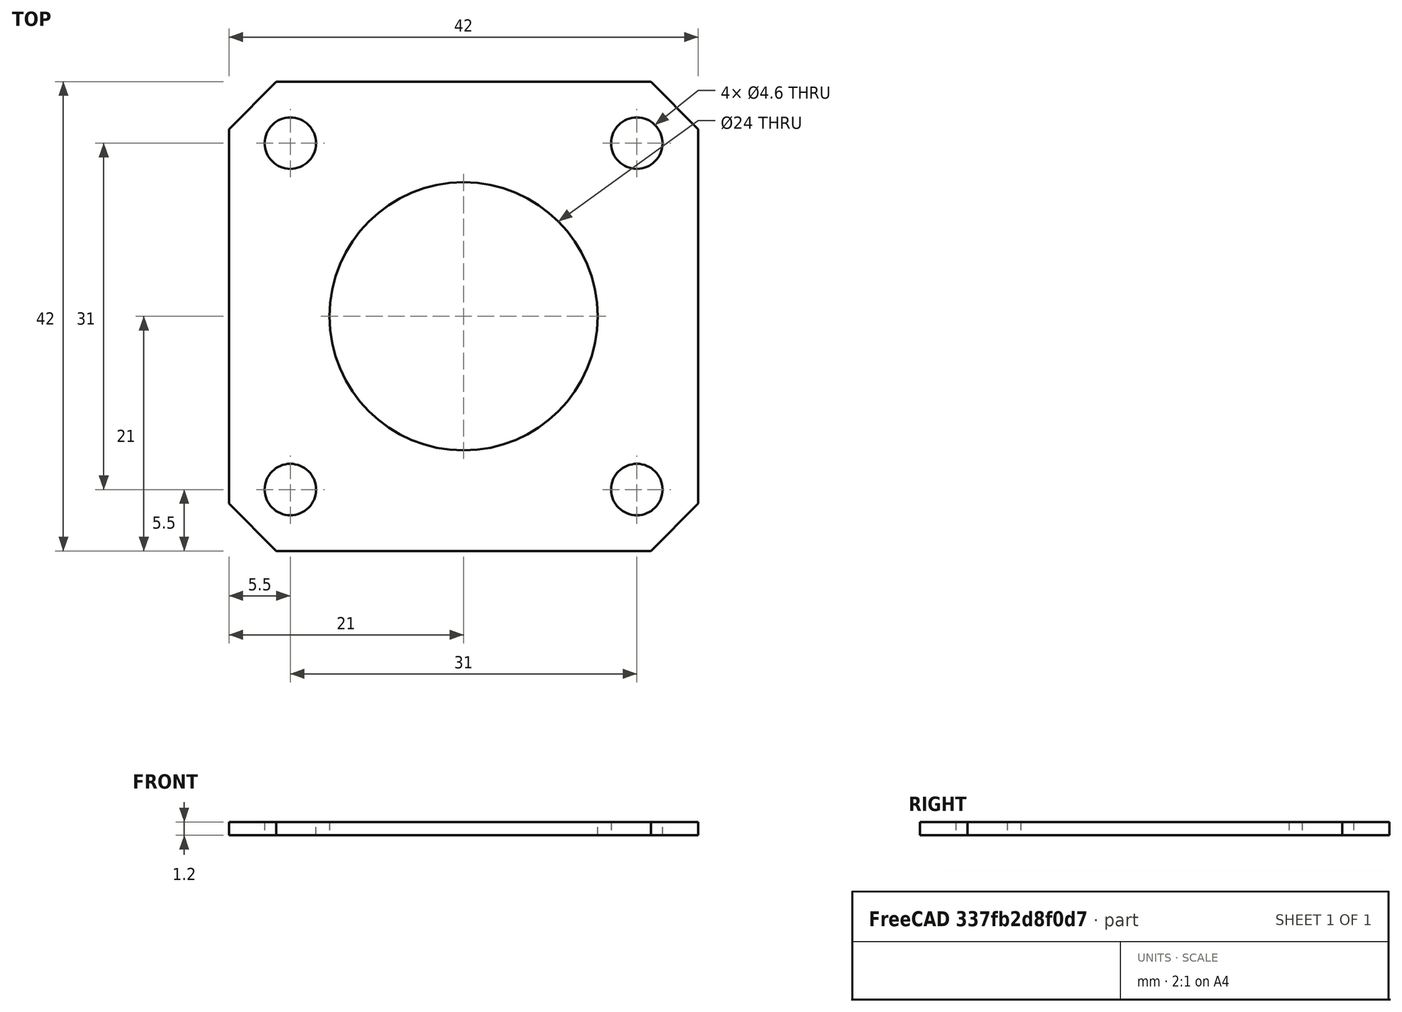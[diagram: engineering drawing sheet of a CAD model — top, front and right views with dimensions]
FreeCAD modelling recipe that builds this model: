
FCSTD DOCUMENT  (FreeCAD 0.20R28936 (Git))
Label: NEMA17_spacer
License: All rights reserved
LicenseURL: http://en.wikipedia.org/wiki/All_rights_reserved
objects: Sketcher::SketchObject×1, PartDesign::Pad×1, PartDesign::Body×1
note: 4 computed .brp shape members not serialized (recipe doc carries the construction recipe); baked Part::Feature solids carry a one-line shape summary decoded from their .brp

FEATURE [Sketcher::SketchObject] Sketch
  FullyConstrained = true
  MapMode = 5
  Support = -> [XY_Plane]
  sketch-geometry (21):
    g0: LineSegment StartX=-16.7574 StartY=21 StartZ=0 EndX=16.7574 EndY=21 EndZ=0
    g1: LineSegment StartX=21 StartY=16.7574 StartZ=0 EndX=21 EndY=-16.7574 EndZ=0
    g2: LineSegment StartX=16.7574 StartY=-21 StartZ=0 EndX=-16.7574 EndY=-21 EndZ=0
    g3: LineSegment StartX=-21 StartY=-16.7574 StartZ=0 EndX=-21 EndY=16.7574 EndZ=0
    g4: LineSegment StartX=-21 StartY=16.7574 StartZ=0 EndX=-16.7574 EndY=21 EndZ=0
    g5: LineSegment StartX=16.7574 StartY=21 StartZ=0 EndX=21 EndY=16.7574 EndZ=0
    g6: LineSegment StartX=16.7574 StartY=-21 StartZ=0 EndX=21 EndY=-16.7574 EndZ=0
    g7: LineSegment StartX=-21 StartY=-16.7574 StartZ=0 EndX=-16.7574 EndY=-21 EndZ=0
    g8: LineSegment StartX=-21 StartY=16.7574 StartZ=0 EndX=21 EndY=-16.7574 EndZ=0
    g9: LineSegment StartX=-16.7574 StartY=21 StartZ=0 EndX=16.7574 EndY=-21 EndZ=0
    g10: LineSegment StartX=-21 StartY=-16.7574 StartZ=0 EndX=21 EndY=16.7574 EndZ=0
    g11: LineSegment StartX=16.7574 StartY=21 StartZ=0 EndX=-16.7574 EndY=-21 EndZ=0
    g12: LineSegment StartX=-15.5 StartY=15.5 StartZ=0 EndX=15.5 EndY=15.5 EndZ=0
    g13: LineSegment StartX=15.5 StartY=15.5 StartZ=0 EndX=15.5 EndY=-15.5 EndZ=0
    g14: LineSegment StartX=15.5 StartY=-15.5 StartZ=0 EndX=-15.5 EndY=-15.5 EndZ=0
    g15: LineSegment StartX=-15.5 StartY=-15.5 StartZ=0 EndX=-15.5 EndY=15.5 EndZ=0
    g16: Circle CenterX=-15.5 CenterY=15.5 CenterZ=0 NormalX=0 NormalY=0 NormalZ=1 AngleXU=0 Radius=2.3
    g17: Circle CenterX=15.5 CenterY=15.5 CenterZ=0 NormalX=0 NormalY=0 NormalZ=1 AngleXU=0 Radius=2.3
    g18: Circle CenterX=15.5 CenterY=-15.5 CenterZ=0 NormalX=0 NormalY=0 NormalZ=1 AngleXU=0 Radius=2.3
    g19: Circle CenterX=-15.5 CenterY=-15.5 CenterZ=0 NormalX=0 NormalY=0 NormalZ=1 AngleXU=0 Radius=2.3
    g20: Circle CenterX=-5.31e-14 CenterY=1.02e-14 CenterZ=0 NormalX=0 NormalY=0 NormalZ=1 AngleXU=0 Radius=12
  constraints (53):
    c: Horizontal(g0)
    c: Horizontal(g2)
    c: Vertical(g1)
    c: Vertical(g3)
    c: Equal(g0,g1)
    c: Equal(g1,g2)
    c: Equal(g2,g3)
    c: Coincident(g4,g3)
    c: Coincident(g4,g0)
    c: Coincident(g5,g0)
    c: Coincident(g5,g1)
    c: Coincident(g6,g2)
    c: Coincident(g6,g1)
    c: Coincident(g7,g3)
    c: Coincident(g7,g2)
    c: Equal(g4,g5)
    c: Equal(g5,g6)
    c: Equal(g6,g7)
    c: Coincident(g8,g3)
    c: Coincident(g8,g1)
    c: Coincident(g9,g0)
    c: Coincident(g9,g2)
    c: Coincident(g10,g3)
    c: Coincident(g10,g1)
    c: Coincident(g11,g0)
    c: Coincident(g11,g2)
    c: Equal(g8,g9)
    c: Equal(g9,g10)
    c: PointOnObject(g20,g10)
    c: PointOnObject(g20,g8)
    c: DistanceX(g3,g1) = 42
    c: Distance(g6) = 6
    c: Coincident(g12,g13)
    c: Coincident(g13,g14)
    c: Coincident(g14,g15)
    c: Coincident(g15,g12)
    c: Horizontal(g12)
    c: Horizontal(g14)
    c: Vertical(g13)
    c: Vertical(g15)
    c: Equal(g12,g15)
    c: DistanceX(g12,g12) = 31
    c: Coincident(g16,g12)
    c: Coincident(g17,g12)
    c: Coincident(g18,g13)
    c: Coincident(g19,g14)
    c: Equal(g16,g17)
    c: Equal(g17,g18)
    c: Equal(g18,g19)
    c: Radius(g16) = 2.3
    c: Radius(g20) = 12
    c: Symmetric(g17,g19,g20)
    c: Coincident(g20,g-1)  '___ANCHOR__'
FEATURE [PartDesign::Pad] Pad
  Direction = (0,0,1)
  Length = 1.2
  Length2 = 10
  Profile = -> Sketch
  ReferenceAxis = -> Sketch [N_Axis]
  Type = 0
FEATURE [PartDesign::Body] Body
  Group = -> [Sketch,Pad]
  Origin = -> Origin
  Tip = -> Pad
